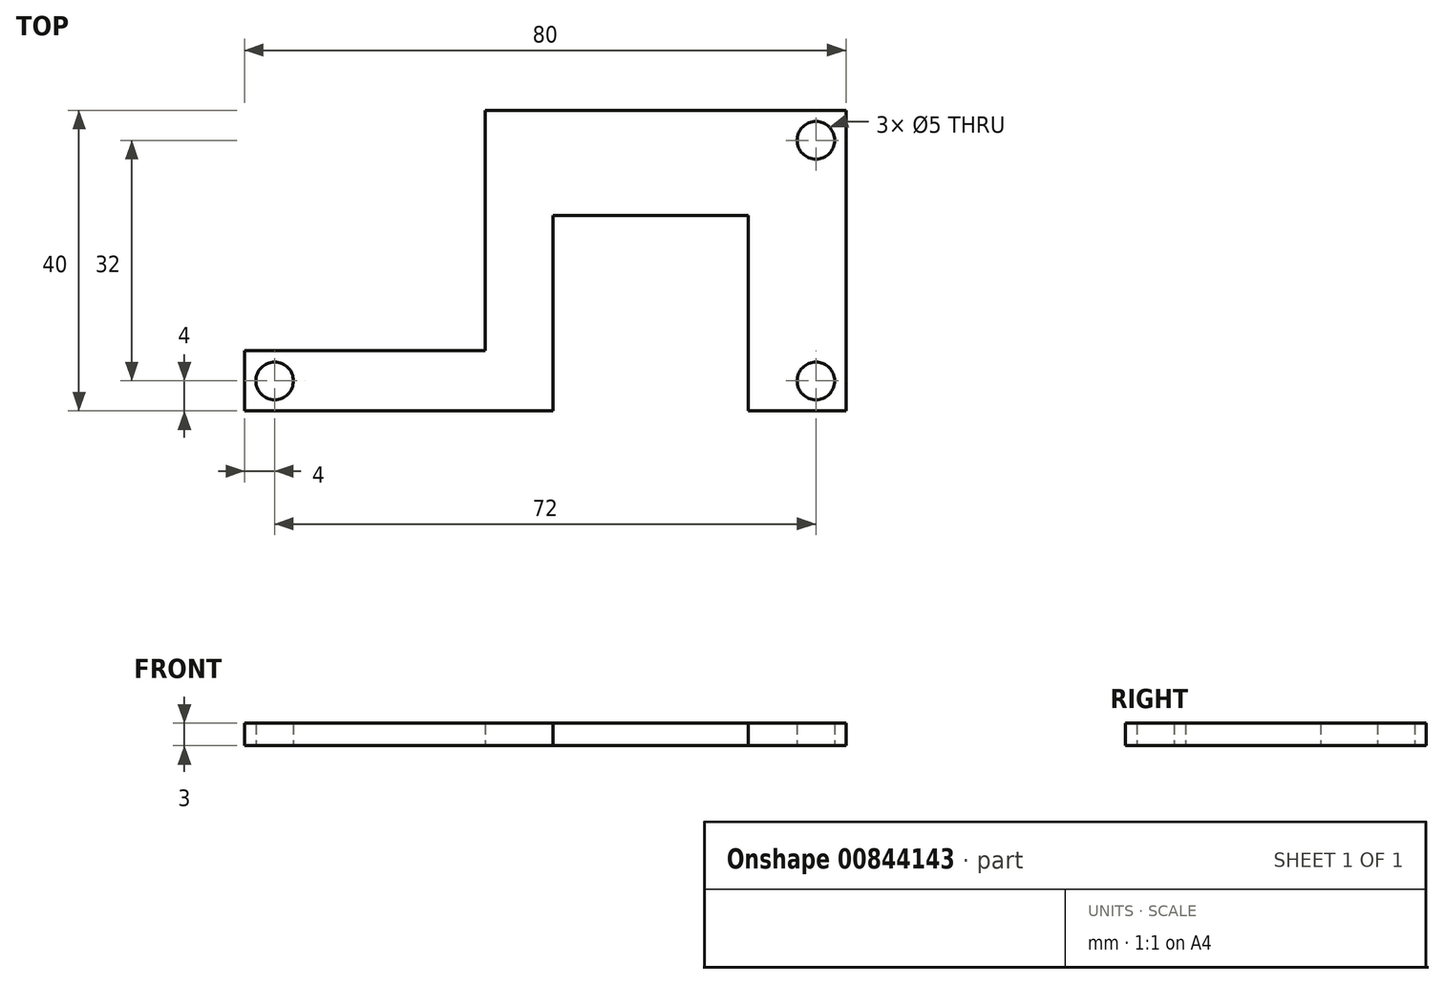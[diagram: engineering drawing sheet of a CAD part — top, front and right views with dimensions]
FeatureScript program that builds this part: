
annotation { "Feature Type Name" : "Feature", "Feature Type Description" : "" }
export const myFeature = defineFeature(function(context is Context, id is Id, definition is map)
    precondition{}
    {
        {
            var Q0;
            Q0=qCreatedBy(makeId("Top.planeOp"),FACE);
            var sketch = newSketch(context, id + "F0", { "sketchPlane" : qUnion([Q0])});
            skLineSegment(sketch, "E0.bottom", {"start": v(0, 0) * mm, "end": v(41, 0) * mm});
            skLineSegment(sketch, "E0.top", {"start": v(32, 40) * mm, "end": v(80, 40) * mm});
            skLineSegment(sketch, "E0.left", {"start": v(0, 0) * mm, "end": v(0, 8) * mm});
            skLineSegment(sketch, "E0.right", {"start": v(80, 0) * mm, "end": v(80, 40) * mm});
            skLineSegment(sketch, "E1.top", {"start": v(0, 8) * mm, "end": v(32, 8) * mm});
            skLineSegment(sketch, "E1.right", {"start": v(32, 40) * mm, "end": v(32, 8) * mm});
            skLineSegment(sketch, "E2.top", {"start": v(41, 26) * mm, "end": v(67, 26) * mm});
            skLineSegment(sketch, "E2.left", {"start": v(41, 0) * mm, "end": v(41, 26) * mm});
            skLineSegment(sketch, "E2.right", {"start": v(67, 0) * mm, "end": v(67, 26) * mm});
            skLineSegment(sketch, "E3.trimOffspring", {"start": v(67, 0) * mm, "end": v(80, 0) * mm});
            skCircle(sketch, "E4", {"center": v(4, 4) * mm, "radius": 2.5 * mm});
            skCircle(sketch, "E5", {"center": v(76, 4) * mm, "radius": 2.5 * mm});
            skCircle(sketch, "E6", {"center": v(76, 36) * mm, "radius": 2.5 * mm});
            skSolve(sketch);
        }
        {
            var Q0;
            Q0=makeQuery(id+"F0.imprint","IMPRINT",FACE,{"disambiguationData":[TD([[makeQuery(id+"F0.imprint","IMPRINT",EDGE,{"derivedFrom":sQuery(id+"F0.wireOp",EDGE,"E0.bottom")}),1.0]])]});
            extrude(context, id + "F1", {"entities" : qUnion([Q0]), "depth" : 3 * mm, "offsetDistance" : 25 * mm});
        }
    });
